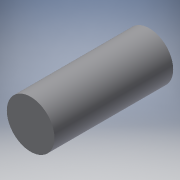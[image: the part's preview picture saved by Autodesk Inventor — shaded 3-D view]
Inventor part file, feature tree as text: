
AUTODESK INVENTOR PART (.ipt)
format: ipt  version: 2018.1 (Build 221171000, 171)  size: 91,648 bytes
history: native  units: mm
features: extrude x1, sketch x1
ambient origin geometry x8: Origin, YZ Plane, XZ Plane, XY Plane, X Axis, Y Axis, Z Axis, Center Point
bodies: Solid1 (feature_tree)
feature tree (2):
  extrude  "Extrusion1"  Depth=50.0mm TaperAngle=0.0deg
  sketch  "Sketch1"  dims[d0=20.06mm d1=50.0mm d2=0.0mm]
